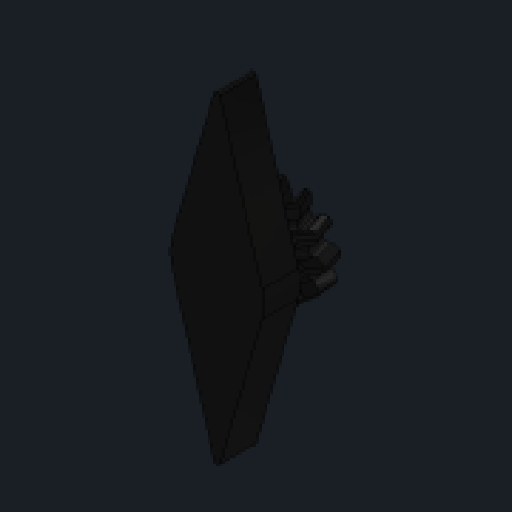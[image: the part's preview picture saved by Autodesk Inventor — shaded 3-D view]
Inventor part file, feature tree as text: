
AUTODESK INVENTOR PART (.ipt)
format: ipt  version: 2023.2 (Build 272271030, 271C)  size: 5,957,632 bytes
history: native  units: mm
features: sketch x4, extrude x4, projected_geometry x3, helix x1, pattern_circular x1, mirror x1, fillet x1
ambient origin geometry x8: Origin, YZ Plane, XZ Plane, XY Plane, X Axis, Y Axis, Z Axis, Center Point
bodies: Solid1 (feature_tree)
feature tree (15):
  sketch  "Sketch1"  dims[d0=2.5mm d1=0.0mm]
  extrude  "Extrusion1"  Depth=10.0mm TaperAngle=0.0deg
  helix  "Coil1"  [1 undecoded]
  pattern_circular  "Circular Pattern1"  [2 undecoded]
  mirror  "Mirror1"
  extrude  "Extrusion2"  [1 undecoded]
  extrude  "Extrusion3"  [1 undecoded]
  fillet  "Fillet1"  [1 undecoded]
  extrude  "Extrusion4"  [1 undecoded]
  sketch  "Sketch2"  dims[d2=110.1mm d3=10.0mm d4=10.0mm d5=0.0mm d6=90.0deg d7=90.0deg d8=0.0mm d9=0.0mm d10=110.0mm d11=360.0deg d13=1.0mm d14=0.0mm d15=47.0mm]
  projected_geometry  "Projected Loop1"
  sketch  "Sketch3"  dims[d16=5.0mm d17=0.0mm]
  projected_geometry  "Projected Loop2"
  sketch  "Sketch4"  dims[d18=0.4mm d19=0.25mm d20=0.0mm]
  projected_geometry  "Projected Loop3"
note: 7 required parameter values undecoded (feature->parameter linkage not recoverable at this tier; creation-order binding heuristic only, values carry confidence <= 0.55)
